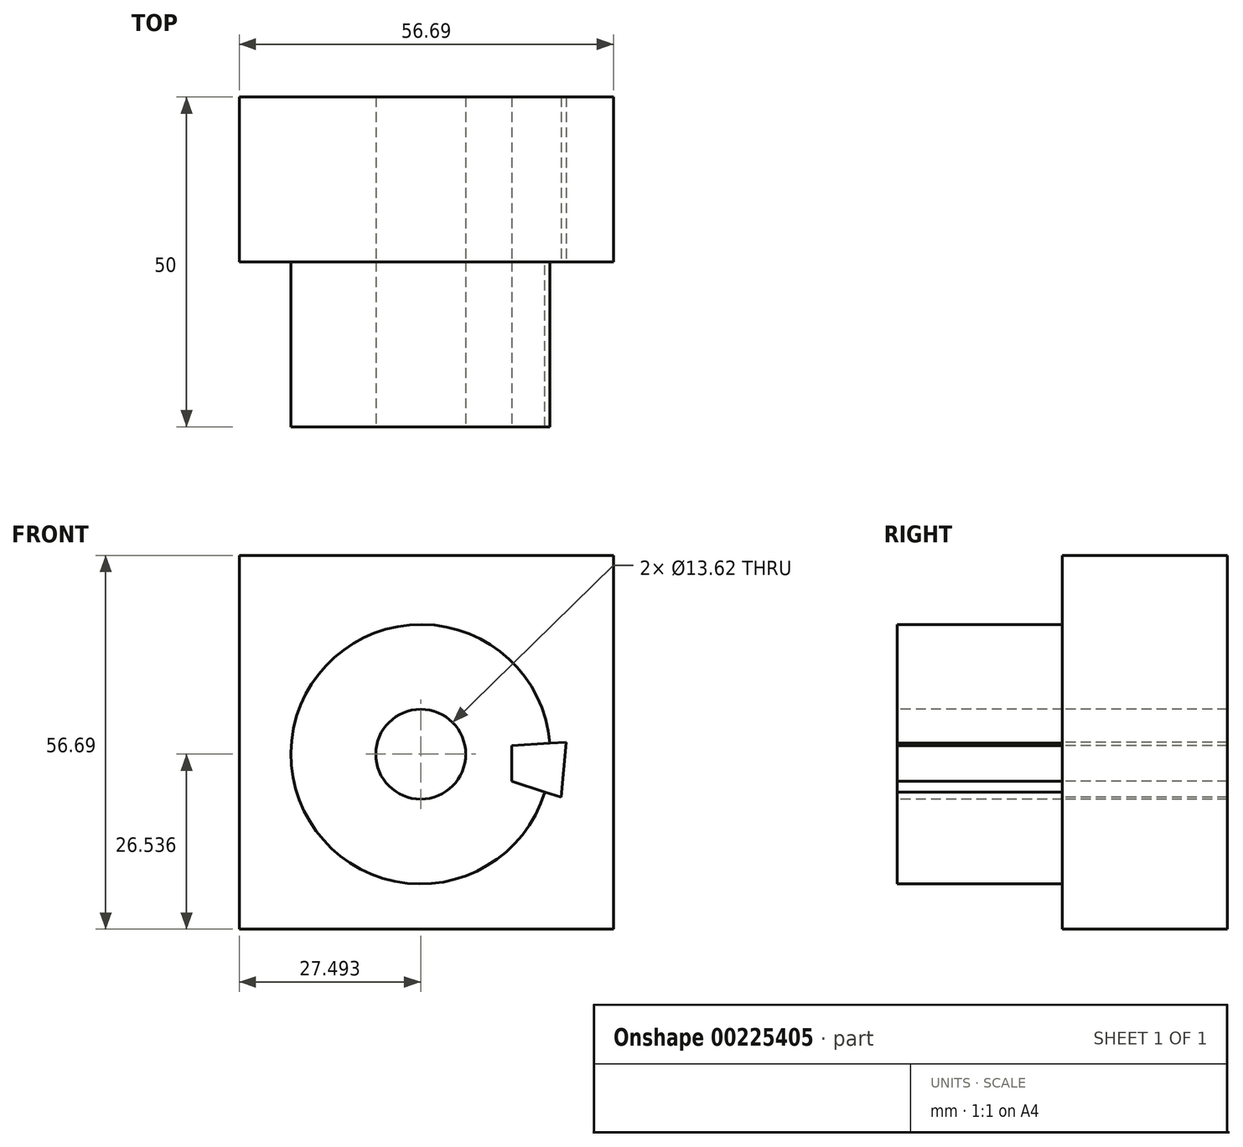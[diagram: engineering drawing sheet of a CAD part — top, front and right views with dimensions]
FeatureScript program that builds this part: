
annotation { "Feature Type Name" : "Feature", "Feature Type Description" : "" }
export const myFeature = defineFeature(function(context is Context, id is Id, definition is map)
    precondition{}
    {
        {
            var Q0;
            Q0=qCreatedBy(makeId("Front.planeOp"),FACE);
            var sketch = newSketch(context, id + "F0", { "sketchPlane" : qUnion([Q0])});
            skLineSegment(sketch, "E0.bottom", {"start": v(-11.86, -5.69) * mm, "end": v(-68.55, -5.69) * mm});
            skLineSegment(sketch, "E0.top", {"start": v(-11.86, 51) * mm, "end": v(-68.55, 51) * mm});
            skLineSegment(sketch, "E0.left", {"start": v(-11.86, -5.69) * mm, "end": v(-11.86, 51) * mm});
            skLineSegment(sketch, "E0.right", {"start": v(-68.55, -5.69) * mm, "end": v(-68.55, 51) * mm});
            skPoint(sketch, "E0.middle", {"position": v(-40.2, 22.66) * mm});
            skSolve(sketch);
        }
        {
            var Q0;
            Q0=makeQuery(id+"F0.imprint","IMPRINT",FACE,{"disambiguationData":[TD([[makeQuery(id+"F0.imprint","IMPRINT",EDGE,{"derivedFrom":sQuery(id+"F0.wireOp",EDGE,"E0.bottom")}),-1.0]])]});
            extrude(context, id + "F1", {"entities" : qUnion([Q0]), "depth" : 25 * mm});
        }
        {
            var Q0;
            Q0=makeQuery(id+"F1.opExtrude","CAP_FACE",FACE,{"disambiguationData":[OSD([sQuery(id+"F0.wireOp",EDGE,"E0.bottom"),sQuery(id+"F0.wireOp",EDGE,"E0.top"),sQuery(id+"F0.wireOp",EDGE,"E0.left"),sQuery(id+"F0.wireOp",EDGE,"E0.right")])],"isStart":false});
            var sketch = newSketch(context, id + "F2", { "sketchPlane" : qUnion([Q0])});
            skCircle(sketch, "E1", {"center": v(-41.06, 20.85) * mm, "radius": 19.67 * mm});
            skSolve(sketch);
        }
        {
            var Q0;
            Q0=makeQuery(id+"F2.imprint","IMPRINT",FACE,{"disambiguationData":[TD([[makeQuery(id+"F2.imprint","IMPRINT",EDGE,{"derivedFrom":sQuery(id+"F2.wireOp",EDGE,"E1")}),1.0]])]});
            extrude(context, id + "F3", {"entities" : qUnion([Q0]), "depth" : 25 * mm});
        }
        {
            var Q0;
            Q0=makeQuery(id+"F3.opExtrude","CAP_FACE",FACE,{"disambiguationData":[OSD([sQuery(id+"F2.wireOp",EDGE,"E1")])],"isStart":false});
            var sketch = newSketch(context, id + "F4", { "sketchPlane" : qUnion([Q0])});
            skCircle(sketch, "E2", {"center": v(-41.06, 20.85) * mm, "radius": 6.81 * mm});
            skSolve(sketch);
        }
        {
            var Q0;
            Q0 = qSketchRegion(id + "F4", true);
            extrude(context, id + "F5", {"entities" : qUnion([Q0]), "operationType" : NewBodyOperationType.REMOVE, "endBound" : BoundingType.THROUGH_ALL, "oppositeDirection" : true, "depth" : 25 * mm});
        }
        {
            var Q0;
            Q0=makeQuery(id+"F3.opExtrude","CAP_FACE",FACE,{"disambiguationData":[OSD([sQuery(id+"F2.wireOp",EDGE,"E1")])],"isStart":false});
            var sketch = newSketch(context, id + "F6", { "sketchPlane" : qUnion([Q0])});
            skLineSegment(sketch, "E3", {"start": v(-27.28, 22.13) * mm, "end": v(-27.28, 16.76) * mm});
            skLineSegment(sketch, "E4", {"start": v(-27.28, 22.13) * mm, "end": v(-19, 22.67) * mm});
            skLineSegment(sketch, "E5", {"start": v(-19, 22.67) * mm, "end": v(-19.8, 14.33) * mm});
            skLineSegment(sketch, "E6", {"start": v(-19.8, 14.33) * mm, "end": v(-27.28, 16.76) * mm});
            skSolve(sketch);
        }
        {
            var Q0;
            Q0 = qSketchRegion(id + "F6", true);
            extrude(context, id + "F7", {"entities" : qUnion([Q0]), "operationType" : NewBodyOperationType.REMOVE, "endBound" : BoundingType.THROUGH_ALL, "oppositeDirection" : true, "depth" : 25 * mm});
        }
    });
